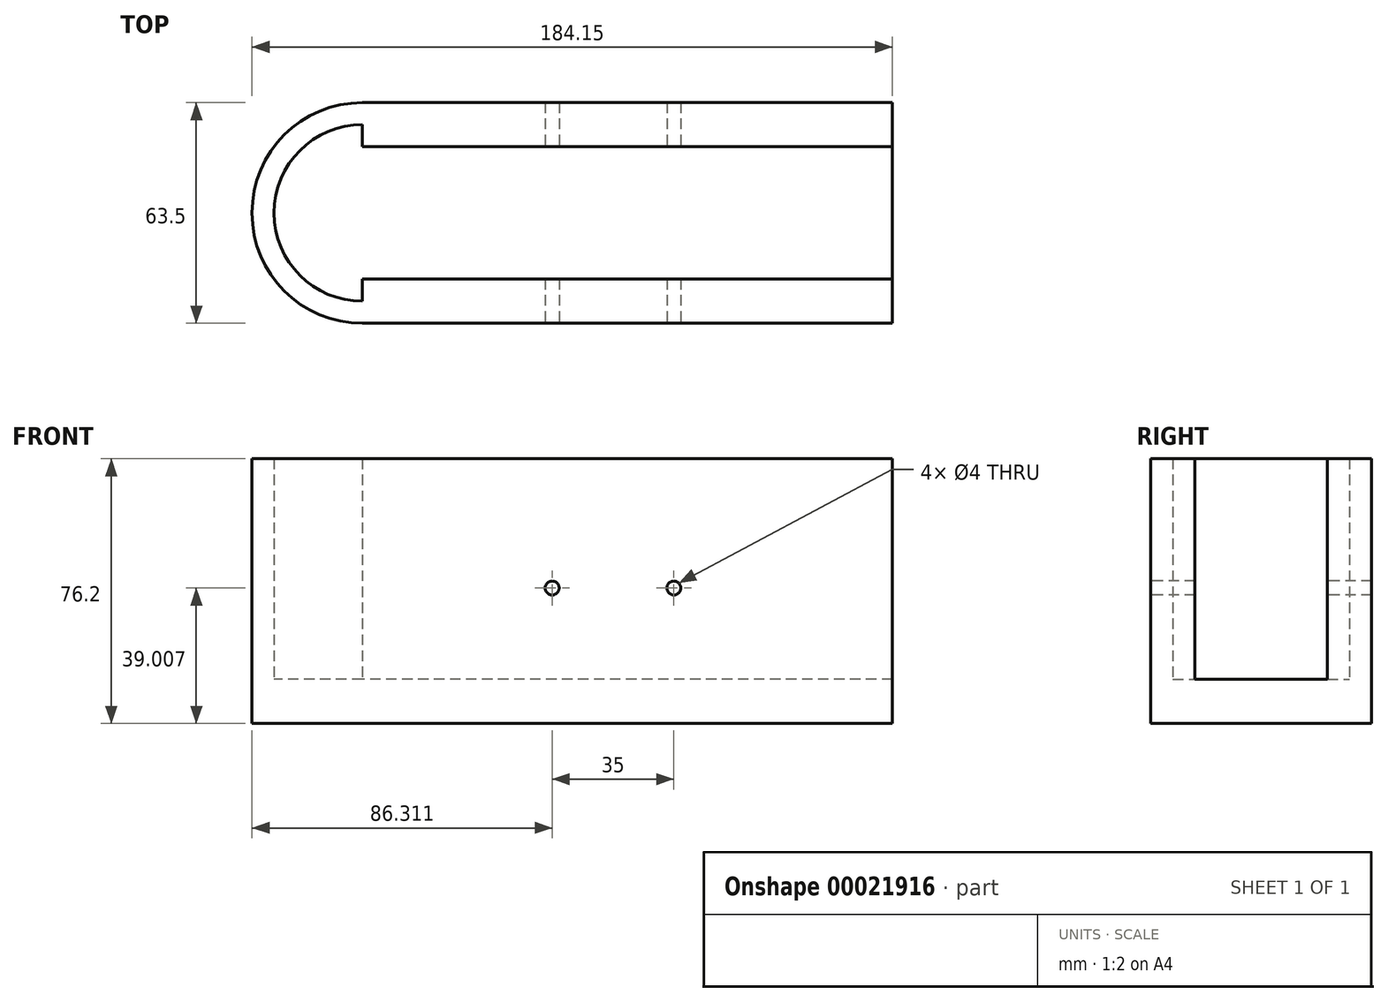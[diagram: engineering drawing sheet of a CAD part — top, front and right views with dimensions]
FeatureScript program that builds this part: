
annotation { "Feature Type Name" : "Feature", "Feature Type Description" : "" }
export const myFeature = defineFeature(function(context is Context, id is Id, definition is map)
    precondition{}
    {
        {
            var Q0;
            Q0=qCreatedBy(makeId("Front.planeOp"),FACE);
            var sketch = newSketch(context, id + "F0", { "sketchPlane" : qUnion([Q0])});
            skLineSegment(sketch, "E0.bottom", {"start": v(-90, 28.4) * mm, "end": v(62.4, 28.4) * mm});
            skLineSegment(sketch, "E0.top", {"start": v(-90, -47.8) * mm, "end": v(62.4, -47.8) * mm});
            skLineSegment(sketch, "E0.left", {"start": v(-90, 28.4) * mm, "end": v(-90, -47.8) * mm});
            skLineSegment(sketch, "E0.right", {"start": v(62.4, 28.4) * mm, "end": v(62.4, -47.8) * mm});
            skSolve(sketch);
        }
        {
            var Q0;
            Q0 = qSketchRegion(id + "F0", true);
            extrude(context, id + "F1", {"entities" : qUnion([Q0]), "depth" : 12.7 * mm});
        }
        {
            var Q0;
            Q0=makeQuery(id+"F1.opExtrude","CAP_FACE",FACE,{"disambiguationData":[OSD([sQuery(id+"F0.wireOp",EDGE,"E0.bottom"),sQuery(id+"F0.wireOp",EDGE,"E0.top"),sQuery(id+"F0.wireOp",EDGE,"E0.left"),sQuery(id+"F0.wireOp",EDGE,"E0.right")])],"isStart":true});
            var sketch = newSketch(context, id + "F2", { "sketchPlane" : qUnion([Q0])});
            skLineSegment(sketch, "E1.bottom", {"start": v(77.3, 28.4) * mm, "end": v(90, 28.4) * mm});
            skLineSegment(sketch, "E1.top", {"start": v(77.3, -47.8) * mm, "end": v(90, -47.8) * mm});
            skLineSegment(sketch, "E1.left", {"start": v(77.3, 28.4) * mm, "end": v(77.3, -47.8) * mm});
            skLineSegment(sketch, "E1.right", {"start": v(90, 28.4) * mm, "end": v(90, -47.8) * mm});
            skSolve(sketch);
        }
        {
            var Q0;
            Q0 = qSketchRegion(id + "F2", true);
            extrude(context, id + "F3", {"entities" : qUnion([Q0]), "operationType" : NewBodyOperationType.ADD, "depth" : 50.8 * mm});
        }
        {
            var Q0;
            Q0=makeQuery(id+"F3.opExtrude","SWEPT_FACE",FACE,{"disambiguationData":[OSD([sQuery(id+"F2.wireOp",EDGE,"E1.left")])]});
            var sketch = newSketch(context, id + "F4", { "sketchPlane" : qUnion([Q0])});
            skLineSegment(sketch, "E2.bottom", {"start": v(38.1, 28.4) * mm, "end": v(50.8, 28.4) * mm});
            skLineSegment(sketch, "E2.top", {"start": v(38.1, -47.8) * mm, "end": v(50.8, -47.8) * mm});
            skLineSegment(sketch, "E2.left", {"start": v(38.1, 28.4) * mm, "end": v(38.1, -47.8) * mm});
            skLineSegment(sketch, "E2.right", {"start": v(50.8, 28.4) * mm, "end": v(50.8, -47.8) * mm});
            skSolve(sketch);
        }
        {
            var Q0;
            Q0 = qSketchRegion(id + "F4", true);
            extrude(context, id + "F5", {"entities" : qUnion([Q0]), "operationType" : NewBodyOperationType.ADD, "depth" : 139.7 * mm});
        }
        {
            var Q0;
            Q0=makeQuery(id+"F3.opExtrude","SWEPT_FACE",FACE,{"disambiguationData":[OSD([sQuery(id+"F2.wireOp",EDGE,"E1.left")])]});
            var sketch = newSketch(context, id + "F6", { "sketchPlane" : qUnion([Q0])});
            skLineSegment(sketch, "E3.bottom", {"start": v(0, -35.1) * mm, "end": v(38.1, -35.1) * mm});
            skLineSegment(sketch, "E3.top", {"start": v(0, -47.8) * mm, "end": v(38.1, -47.8) * mm});
            skLineSegment(sketch, "E3.left", {"start": v(0, -35.1) * mm, "end": v(0, -47.8) * mm});
            skLineSegment(sketch, "E3.right", {"start": v(38.1, -35.1) * mm, "end": v(38.1, -47.8) * mm});
            skSolve(sketch);
        }
        {
            var Q0;
            Q0 = qSketchRegion(id + "F6", true);
            extrude(context, id + "F7", {"entities" : qUnion([Q0]), "operationType" : NewBodyOperationType.ADD, "depth" : 139.7 * mm});
        }
        {
            var Q0;
            Q0=makeQuery(id+"F1.opExtrude","CAP_FACE",FACE,{"disambiguationData":[OSD([sQuery(id+"F0.wireOp",EDGE,"E0.bottom"),sQuery(id+"F0.wireOp",EDGE,"E0.top"),sQuery(id+"F0.wireOp",EDGE,"E0.left"),sQuery(id+"F0.wireOp",EDGE,"E0.right")])],"isStart":false});
            var sketch = newSketch(context, id + "F8", { "sketchPlane" : qUnion([Q0])});
            skLineSegment(sketch, "E4", {"start": v(-35.43, -8.8) * mm, "end": v(-0.43, -8.8) * mm});
            skCircle(sketch, "E5", {"center": v(-35.43, -8.8) * mm, "radius": 2 * mm});
            skCircle(sketch, "E6", {"center": v(-0.43, -8.8) * mm, "radius": 2 * mm});
            skSolve(sketch);
        }
        {
            var Q0;
            Q0 = qSketchRegion(id + "F8", true);
            extrude(context, id + "F9", {"entities" : qUnion([Q0]), "operationType" : NewBodyOperationType.REMOVE, "endBound" : BoundingType.THROUGH_ALL, "oppositeDirection" : true, "depth" : 25.4 * mm});
        }
        {
            var Q0;
            Q0=makeQuery(id+"F3.boolean.opBoolean","MERGE",FACE,{"derivedFrom":[makeQuery(id+"F1.opExtrude","SWEPT_FACE",FACE,{"disambiguationData":[OSD([sQuery(id+"F0.wireOp",EDGE,"E0.left")])]}),makeQuery(id+"F3.opExtrude","SWEPT_FACE",FACE,{"disambiguationData":[OSD([sQuery(id+"F2.wireOp",EDGE,"E1.right")])]})]});
            var sketch = newSketch(context, id + "F10", { "sketchPlane" : qUnion([Q0])});
            skLineSegment(sketch, "E7.bottom", {"start": v(-38.1, 28.4) * mm, "end": v(0, 28.4) * mm});
            skLineSegment(sketch, "E7.top", {"start": v(-38.1, -35.1) * mm, "end": v(0, -35.1) * mm});
            skLineSegment(sketch, "E7.left", {"start": v(-38.1, 28.4) * mm, "end": v(-38.1, -35.1) * mm});
            skLineSegment(sketch, "E7.right", {"start": v(0, 28.4) * mm, "end": v(0, -35.1) * mm});
            skPoint(sketch, "E8", {"position": v(12.7, 28.4) * mm});
            skPoint(sketch, "E9", {"position": v(-50.8, 28.4) * mm});
            skPoint(sketch, "E10", {"position": v(0, -47.8) * mm});
            skSolve(sketch);
        }
        {
            var Q0;
            Q0 = qSketchRegion(id + "F10", true);
            extrude(context, id + "F11", {"entities" : qUnion([Q0]), "operationType" : NewBodyOperationType.REMOVE, "oppositeDirection" : true, "depth" : 12.7 * mm});
        }
        {
            var Q0;
            Q0=makeQuery(id+"F7.boolean.opBoolean","MERGE",FACE,{"derivedFrom":[makeQuery(id+"F5.boolean.opBoolean","MERGE",FACE,{"derivedFrom":[makeQuery(id+"F3.boolean.opBoolean","MERGE",FACE,{"derivedFrom":[makeQuery(id+"F1.opExtrude","SWEPT_FACE",FACE,{"disambiguationData":[OSD([sQuery(id+"F0.wireOp",EDGE,"E0.top")])]}),makeQuery(id+"F3.opExtrude","SWEPT_FACE",FACE,{"disambiguationData":[OSD([sQuery(id+"F2.wireOp",EDGE,"E1.top")])]})]}),makeQuery(id+"F5.opExtrude","SWEPT_FACE",FACE,{"disambiguationData":[OSD([sQuery(id+"F4.wireOp",EDGE,"E2.top")])]})]}),makeQuery(id+"F7.opExtrude","SWEPT_FACE",FACE,{"disambiguationData":[OSD([sQuery(id+"F6.wireOp",EDGE,"E3.top")])]})]});
            var sketch = newSketch(context, id + "F12", { "sketchPlane" : qUnion([Q0])});
            skCircle(sketch, "E11", {"center": v(-90, -19.05) * mm, "radius": 31.75 * mm});
            skCircle(sketch, "E12", {"center": v(-90, -19.05) * mm, "radius": 25.4 * mm});
            skSolve(sketch);
        }
        {
            var Q0;
            {var subQ0=sQuery(id+"F0.wireOp",EDGE,"E0.top");var subQ1=sQuery(id+"F2.wireOp",EDGE,"E1.top");var subQ2=makeQuery(id+"F3.boolean.opBoolean","MERGE",EDGE,{"derivedFrom":[makeQuery(id+"F1.opExtrude","SWEPT_EDGE",EDGE,{"disambiguationData":[OSD([subQ0,sQuery(id+"F0.wireOp",EDGE,"E0.left")])]}),makeQuery(id+"F3.opExtrude","SWEPT_EDGE",EDGE,{"disambiguationData":[OSD([subQ1,sQuery(id+"F2.wireOp",EDGE,"E1.right")])]})]});var subQ3=sQuery(id+"F12.wireOp",EDGE,"E12");var subQ7=makeQuery(id+"F12.imprint","INTERSECT",VERTEX,{"disambiguationData":[OD(0.0)],"derivedFrom":[subQ2,subQ3]});Q0=makeQuery(id+"F12.imprint","IMPRINT",FACE,{"disambiguationData":[TD([[makeQuery(id+"F12.imprint","IMPRINT",EDGE,{"disambiguationData":[TD([[subQ7,-1.0]])],"derivedFrom":subQ3}),-1.0]])]});}
            extrude(context, id + "F13", {"entities" : qUnion([Q0]), "operationType" : NewBodyOperationType.ADD, "oppositeDirection" : true, "depth" : 76.2 * mm});
        }
        {
            var Q0;
            {var subQ0=sQuery(id+"F0.wireOp",EDGE,"E0.top");var subQ1=sQuery(id+"F2.wireOp",EDGE,"E1.top");Q0=makeQuery(id+"F13.boolean.opBoolean","MERGE",FACE,{"derivedFrom":[makeQuery(id+"F7.boolean.opBoolean","MERGE",FACE,{"derivedFrom":[makeQuery(id+"F5.boolean.opBoolean","MERGE",FACE,{"derivedFrom":[makeQuery(id+"F3.boolean.opBoolean","MERGE",FACE,{"derivedFrom":[makeQuery(id+"F1.opExtrude","SWEPT_FACE",FACE,{"disambiguationData":[OSD([subQ0])]}),makeQuery(id+"F3.opExtrude","SWEPT_FACE",FACE,{"disambiguationData":[OSD([subQ1])]})]}),makeQuery(id+"F5.opExtrude","SWEPT_FACE",FACE,{"disambiguationData":[OSD([sQuery(id+"F4.wireOp",EDGE,"E2.top")])]})]}),makeQuery(id+"F7.opExtrude","SWEPT_FACE",FACE,{"disambiguationData":[OSD([sQuery(id+"F6.wireOp",EDGE,"E3.top")])]})]}),makeQuery(id+"F13.opExtrude","CAP_FACE",FACE,{"disambiguationData":[OSD([subQ0,sQuery(id+"F0.wireOp",EDGE,"E0.left"),subQ1,sQuery(id+"F2.wireOp",EDGE,"E1.right"),sQuery(id+"F12.wireOp",EDGE,"E11"),sQuery(id+"F12.wireOp",EDGE,"E12")])],"isStart":true})]});}
            var sketch = newSketch(context, id + "F14", { "sketchPlane" : qUnion([Q0])});
            skCircle(sketch, "E13", {"center": v(-90, -19.05) * mm, "radius": 25.4 * mm});
            skSolve(sketch);
        }
        {
            var Q0;
            {var subQ0=makeQuery(id+"F3.boolean.opBoolean","MERGE",EDGE,{"derivedFrom":[makeQuery(id+"F1.opExtrude","SWEPT_EDGE",EDGE,{"disambiguationData":[OSD([sQuery(id+"F0.wireOp",EDGE,"E0.top"),sQuery(id+"F0.wireOp",EDGE,"E0.left")])]}),makeQuery(id+"F3.opExtrude","SWEPT_EDGE",EDGE,{"disambiguationData":[OSD([sQuery(id+"F2.wireOp",EDGE,"E1.top"),sQuery(id+"F2.wireOp",EDGE,"E1.right")])]})]});Q0=makeQuery(id+"F14.imprint","IMPRINT",FACE,{"disambiguationData":[TD([[makeQuery(id+"F14.imprint","IMPRINT",EDGE,{"derivedFrom":subQ0}),-1.0]])]});}
            extrude(context, id + "F15", {"entities" : qUnion([Q0]), "operationType" : NewBodyOperationType.ADD, "oppositeDirection" : true, "depth" : 12.7 * mm});
        }
    });
